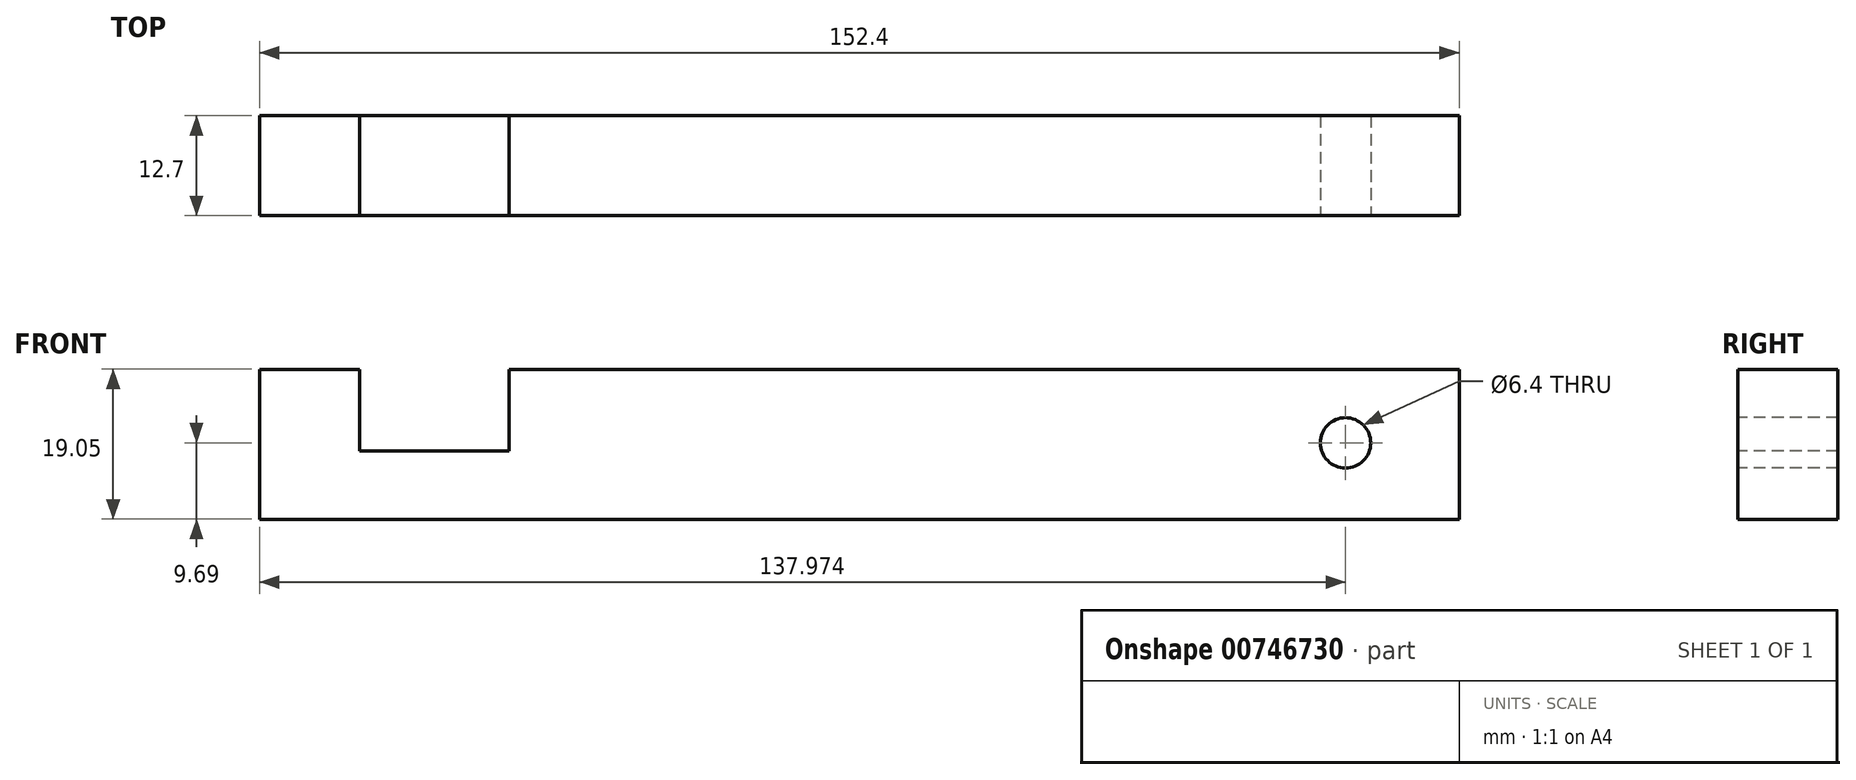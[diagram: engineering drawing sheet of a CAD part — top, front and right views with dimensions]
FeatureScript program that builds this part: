
annotation { "Feature Type Name" : "Feature", "Feature Type Description" : "" }
export const myFeature = defineFeature(function(context is Context, id is Id, definition is map)
    precondition{}
    {
        {
            var Q0;
            Q0=qCreatedBy(makeId("Right.planeOp"),FACE);
            var sketch = newSketch(context, id + "F0", { "sketchPlane" : qUnion([Q0])});
            skLineSegment(sketch, "E0.bottom", {"start": v(-4.07, 9.36) * mm, "end": v(8.63, 9.36) * mm});
            skLineSegment(sketch, "E0.top", {"start": v(-4.07, -9.7) * mm, "end": v(8.63, -9.7) * mm});
            skLineSegment(sketch, "E0.left", {"start": v(-4.07, 9.36) * mm, "end": v(-4.07, -9.7) * mm});
            skLineSegment(sketch, "E0.right", {"start": v(8.63, 9.36) * mm, "end": v(8.63, -9.7) * mm});
            skSolve(sketch);
        }
        {
            var Q0;
            Q0=makeQuery(id+"F0.imprint","IMPRINT",FACE,{"disambiguationData":[TD([[makeQuery(id+"F0.imprint","IMPRINT",EDGE,{"derivedFrom":sQuery(id+"F0.wireOp",EDGE,"E0.bottom")}),-1.0]])]});
            extrude(context, id + "F1", {"entities" : qUnion([Q0]), "depth" : 152.4 * mm, "offsetDistance" : 25.4 * mm});
        }
        {
            var Q0;
            Q0=makeQuery(id+"F1.opExtrude","SWEPT_FACE",FACE,{"disambiguationData":[OSD([sQuery(id+"F0.wireOp",EDGE,"E0.left")])]});
            var sketch = newSketch(context, id + "F2", { "sketchPlane" : qUnion([Q0])});
            skLineSegment(sketch, "E1.bottom", {"start": v(12.7, 9.36) * mm, "end": v(31.75, 9.36) * mm});
            skLineSegment(sketch, "E1.top", {"start": v(12.7, -1) * mm, "end": v(31.75, -1) * mm});
            skLineSegment(sketch, "E1.left", {"start": v(12.7, 9.36) * mm, "end": v(12.7, -1) * mm});
            skLineSegment(sketch, "E1.right", {"start": v(31.75, 9.36) * mm, "end": v(31.75, -1) * mm});
            skSolve(sketch);
        }
        {
            var Q0;
            Q0=makeQuery(id+"F2.imprint","IMPRINT",FACE,{"disambiguationData":[TD([[makeQuery(id+"F2.imprint","IMPRINT",EDGE,{"derivedFrom":sQuery(id+"F2.wireOp",EDGE,"E1.bottom")}),1.0]])]});
            extrude(context, id + "F3", {"entities" : qUnion([Q0]), "operationType" : NewBodyOperationType.REMOVE, "oppositeDirection" : true, "depth" : 25.4 * mm, "offsetDistance" : 25.4 * mm});
        }
        {
            var Q0;
            Q0=makeQuery(id+"F1.opExtrude","SWEPT_FACE",FACE,{"disambiguationData":[OSD([sQuery(id+"F0.wireOp",EDGE,"E0.left")])]});
            var sketch = newSketch(context, id + "F4", { "sketchPlane" : qUnion([Q0])});
            skCircle(sketch, "E2", {"center": v(137.97, 0) * mm, "radius": 9.36 * mm});
            skSolve(sketch);
        }
        {
            var Q0;
            Q0=sQuery(id+"F4.wireOp",VERTEX,"E2.center");
            var Q1;
            Q1=makeQuery(id+"F1.opExtrude","SWEPT_BODY",BODY,{"disambiguationData":[OSD([sQuery(id+"F0.wireOp",EDGE,"E0.bottom"),sQuery(id+"F0.wireOp",EDGE,"E0.top"),sQuery(id+"F0.wireOp",EDGE,"E0.left"),sQuery(id+"F0.wireOp",EDGE,"E0.right")])]});
            hole(context, id + "F5", {"style" : HoleStyle.SIMPLE, "endStyle" : HoleEndStyle.THROUGH, "holeDiameter" : 6.4 * mm, "majorDiameter" : 6.35 * mm, "isTappedThrough" : true, "tappedDepth" : 12.7 * mm, "tapClearance" : 3, "locations" : qUnion([Q0]), "scope" : qUnion([Q1])});
        }
    });
